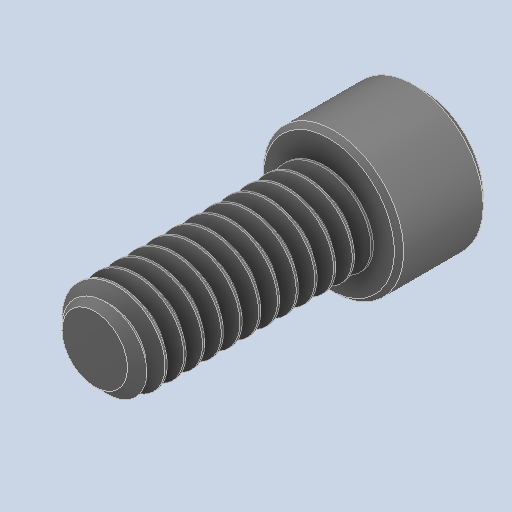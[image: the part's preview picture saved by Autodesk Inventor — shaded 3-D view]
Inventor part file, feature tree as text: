
AUTODESK INVENTOR PART (.ipt)
format: ipt  version: 2024.2 (Build 282272000, 272)  size: 538,624 bytes
history: native  units: in
note: dims shown in document units (in); Inventor stores cm internally (conversion verified against a paired STEP export)
features: chamfer x1
ambient origin geometry x8: Origin, YZ Plane, XZ Plane, XY Plane, X Axis, Y Axis, Z Axis, Center Point
bodies: Solid1 (feature_tree)
feature tree (1):
  chamfer  "Chamfer2"  [1 undecoded]
note: 1 required parameter value undecoded (feature->parameter linkage not recoverable at this tier; creation-order binding heuristic only, values carry confidence <= 0.55)
